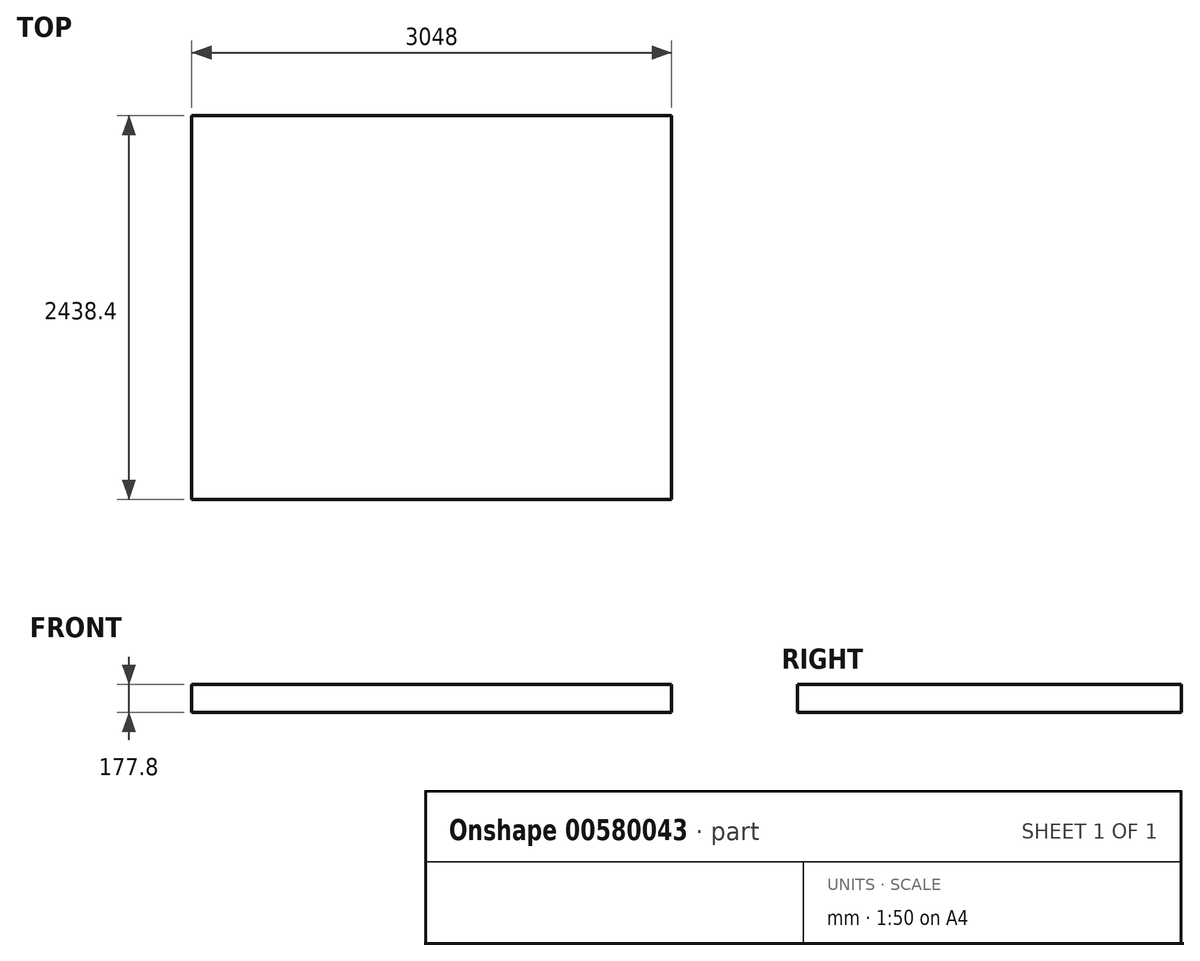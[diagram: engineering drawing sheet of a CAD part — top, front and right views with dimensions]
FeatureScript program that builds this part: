
annotation { "Feature Type Name" : "Feature", "Feature Type Description" : "" }
export const myFeature = defineFeature(function(context is Context, id is Id, definition is map)
    precondition{}
    {
        {
            var Q0;
            Q0=qCreatedBy(makeId("Top.planeOp"),FACE);
            var sketch = newSketch(context, id + "F0", { "sketchPlane" : qUnion([Q0])});
            skLineSegment(sketch, "E0.bottom", {"start": v(-915.7, 1579.5) * mm, "end": v(2132.3, 1579.5) * mm});
            skLineSegment(sketch, "E0.top", {"start": v(-915.7, -858.9) * mm, "end": v(2132.3, -858.9) * mm});
            skLineSegment(sketch, "E0.left", {"start": v(-915.7, 1579.5) * mm, "end": v(-915.7, -858.9) * mm});
            skLineSegment(sketch, "E0.right", {"start": v(2132.3, 1579.5) * mm, "end": v(2132.3, -858.9) * mm});
            skSolve(sketch);
        }
        {
            var Q0;
            Q0 = qSketchRegion(id + "F0", true);
            extrude(context, id + "F1", {"entities" : qUnion([Q0]), "depth" : 177.8 * mm, "offsetDistance" : 30.48 * mm});
        }
    });
